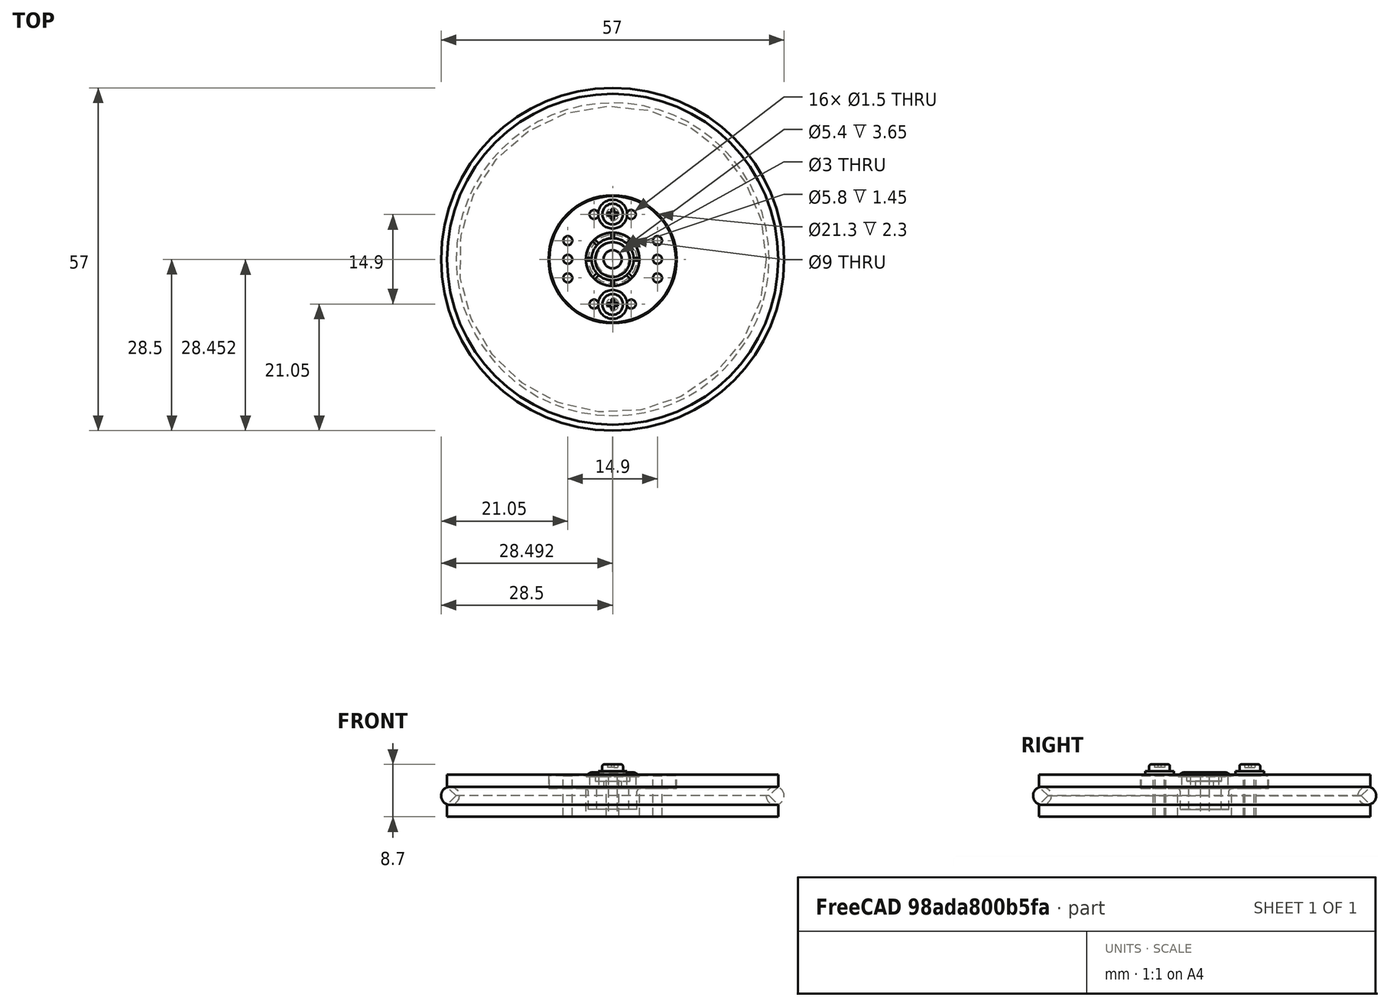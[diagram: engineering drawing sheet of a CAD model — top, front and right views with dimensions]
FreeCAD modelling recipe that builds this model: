
FCSTD DOCUMENT  (FreeCAD 0.14R3702 (Git))
Label: Miniskybot-wheel-rounded-horn-asembly
License: CC-BY 3.0
LicenseURL: http://creativecommons.org/licenses/by/3.0/
objects: Part::Feature×3, Part::Torus×1, Part::Mirroring×1, Part::Compound×1
note: 6 computed .brp shape members not serialized (recipe doc carries the construction recipe); baked Part::Feature solids carry a one-line shape summary decoded from their .brp

FEATURE [Part::Feature] Fillet  label="servo-rounded-horn"
  Placement = pos=(0,0,-2.3) rot=(1,0,0;1.5708rad)
  shape: bbox 21 x 21 x 6.2 mm, 65 faces (baked)
FEATURE [Part::Feature] PolarPattern001  label="Wheel-rounded-horn"
  Placement = pos=(0,0,0) rot=(1,0,0;1.5708rad)
  shape: bbox 55 x 55 x 7 mm, 13 faces (baked)
FEATURE [Part::Torus] Torus  label="o-ring"
  Angle1 = -180
  Angle2 = 180
  Angle3 = 360
  Radius1 = 27
  Radius2 = 1.5
FEATURE [Part::Feature] Fillet002  label="bolt-1"
  Placement = pos=(0,7.5,3.5) rot=(0,0,1;0rad)
  shape: bbox 4.8 x 4.8 x 8.7 mm, 21 faces (baked)
FEATURE [Part::Mirroring] Part__Mirroring  label="bolt-2"
  Base = (0,0,0)
  Normal = (0,1,0)
  Source = -> Fillet002
FEATURE [Part::Compound] Compound  label="Miniskybot-wheel-rounded-horn-assembly"
  Links = -> [Fillet,PolarPattern001,Torus,Part__Mirroring,Fillet002]
